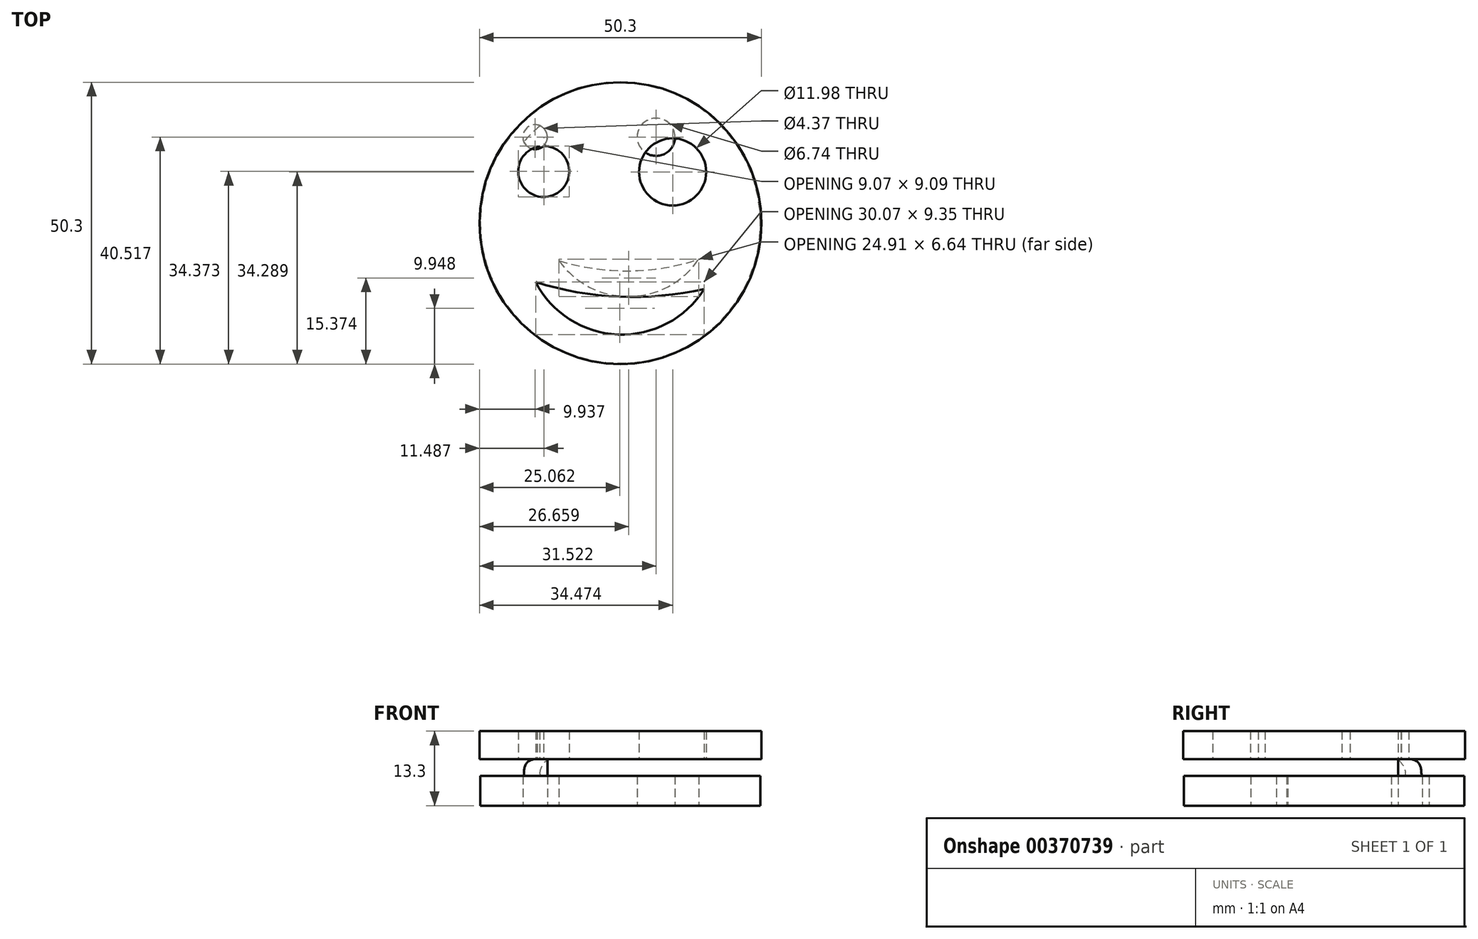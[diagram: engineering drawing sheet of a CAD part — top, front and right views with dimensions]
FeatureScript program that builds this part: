
annotation { "Feature Type Name" : "Feature", "Feature Type Description" : "" }
export const myFeature = defineFeature(function(context is Context, id is Id, definition is map)
    precondition{}
    {
        {
            var Q0;
            Q0=qCreatedBy(makeId("Top.planeOp"),FACE);
            var sketch = newSketch(context, id + "F0", { "sketchPlane" : qUnion([Q0])});
            skCircle(sketch, "E0", {"center": v(0, 0) * mm, "radius": 25 * mm});
            skCircle(sketch, "E1", {"center": v(-15.21, 15.37) * mm, "radius": 2.19 * mm});
            skCircle(sketch, "E2", {"center": v(6.37, 15.37) * mm, "radius": 3.37 * mm});
            skArc(sketch, "E3", {"start": v(-10.94, -6.7) * mm, "mid": v(1.57, -13.1) * mm, "end": v(13.96, -6.46) * mm});
            skArc(sketch, "E4", {"start": v(-10.94, -6.7) * mm, "mid": v(1.53, -8.53) * mm, "end": v(13.96, -6.46) * mm});
            skSolve(sketch);
        }
        {
            var Q0;
            Q0=makeQuery(id+"F0.imprint","IMPRINT",FACE,{"disambiguationData":[TD([[makeQuery(id+"F0.imprint","IMPRINT",EDGE,{"derivedFrom":sQuery(id+"F0.wireOp",EDGE,"E0")}),1.0]])]});
            extrude(context, id + "F1", {"entities" : qUnion([Q0]), "depth" : 5.3 * mm});
        }
        {
            var Q0;
            Q0=makeQuery(id+"F1.opExtrude","CAP_FACE",FACE,{"disambiguationData":[OSD([sQuery(id+"F0.wireOp",EDGE,"E0")])],"isStart":false});
            var sketch = newSketch(context, id + "F2", { "sketchPlane" : qUnion([Q0])});
            skCircle(sketch, "E5", {"center": v(0, 0) * mm, "radius": 22.52 * mm});
            skSolve(sketch);
        }
        {
            var Q0;
            Q0=makeQuery(id+"F2.imprint","IMPRINT",FACE,{"disambiguationData":[TD([[makeQuery(id+"F2.imprint","IMPRINT",EDGE,{"derivedFrom":sQuery(id+"F2.wireOp",EDGE,"E5")}),1.0]])]});
            extrude(context, id + "F3", {"entities" : qUnion([Q0]), "depth" : 3 * mm});
        }
        {
            var Q0;
            Q0=makeQuery(id+"F3.opExtrude","CAP_EDGE",EDGE,{"disambiguationData":[OSD([sQuery(id+"F2.wireOp",EDGE,"E5")])],"isStart":false});
            fillet(context, id + "F4", {"entities" : qUnion([Q0]), "radius" : 2.66 * mm, "tangentPropagation" : true, "allowEdgeOverflow" : false});
        }
        {
            var Q0;
            Q0=makeQuery(id+"F3.opExtrude","CAP_FACE",FACE,{"disambiguationData":[OSD([sQuery(id+"F2.wireOp",EDGE,"E5")])],"isStart":false});
            var sketch = newSketch(context, id + "F5", { "sketchPlane" : qUnion([Q0])});
            skCircle(sketch, "E6", {"center": v(0, 0) * mm, "radius": 25.15 * mm});
            skCircle(sketch, "E7", {"center": v(-13.68, 9.22) * mm, "radius": 4.55 * mm});
            skPoint(sketch, "E7.centerSnap0", {"position": v(-13.68, 13.81) * mm});
            skCircle(sketch, "E8", {"center": v(9.32, 9.14) * mm, "radius": 6 * mm});
            skArc(sketch, "E9", {"start": v(-15.12, -10.53) * mm, "mid": v(-0.45, -19.88) * mm, "end": v(14.94, -11.76) * mm});
            skArc(sketch, "E10", {"start": v(-15.12, -10.53) * mm, "mid": v(-0.17, -13.13) * mm, "end": v(14.94, -11.76) * mm});
            skSolve(sketch);
        }
        {
            var Q0;
            Q0=makeQuery(id+"F5.imprint","IMPRINT",FACE,{"disambiguationData":[TD([[makeQuery(id+"F5.imprint","IMPRINT",EDGE,{"derivedFrom":sQuery(id+"F5.wireOp",EDGE,"E6")}),1.0]])]});
            var Q1;
            {var subQ0=sQuery(id+"F2.wireOp",EDGE,"E5");Q1=makeQuery(id+"F5.imprint","IMPRINT",FACE,{"disambiguationData":[TD([[makeQuery(id+"F5.imprint","IMPRINT",EDGE,{"derivedFrom":makeQuery(id+"F4.opFillet","BLEND_EDGE",EDGE,{"blendedFrom":[makeQuery(id+"F3.opExtrude","CAP_EDGE",EDGE,{"disambiguationData":[OSD([subQ0])],"isStart":false}),makeQuery(id+"F3.opExtrude","CAP_FACE",FACE,{"disambiguationData":[OSD([subQ0])],"isStart":false})],"blendedInto":[makeQuery(id+"F3.opExtrude","CAP_FACE",FACE,{"disambiguationData":[OSD([subQ0])],"isStart":false})]})}),1.0]])]});}
            extrude(context, id + "F6", {"entities" : qUnion([Q0, Q1]), "depth" : 5 * mm});
        }
    });
